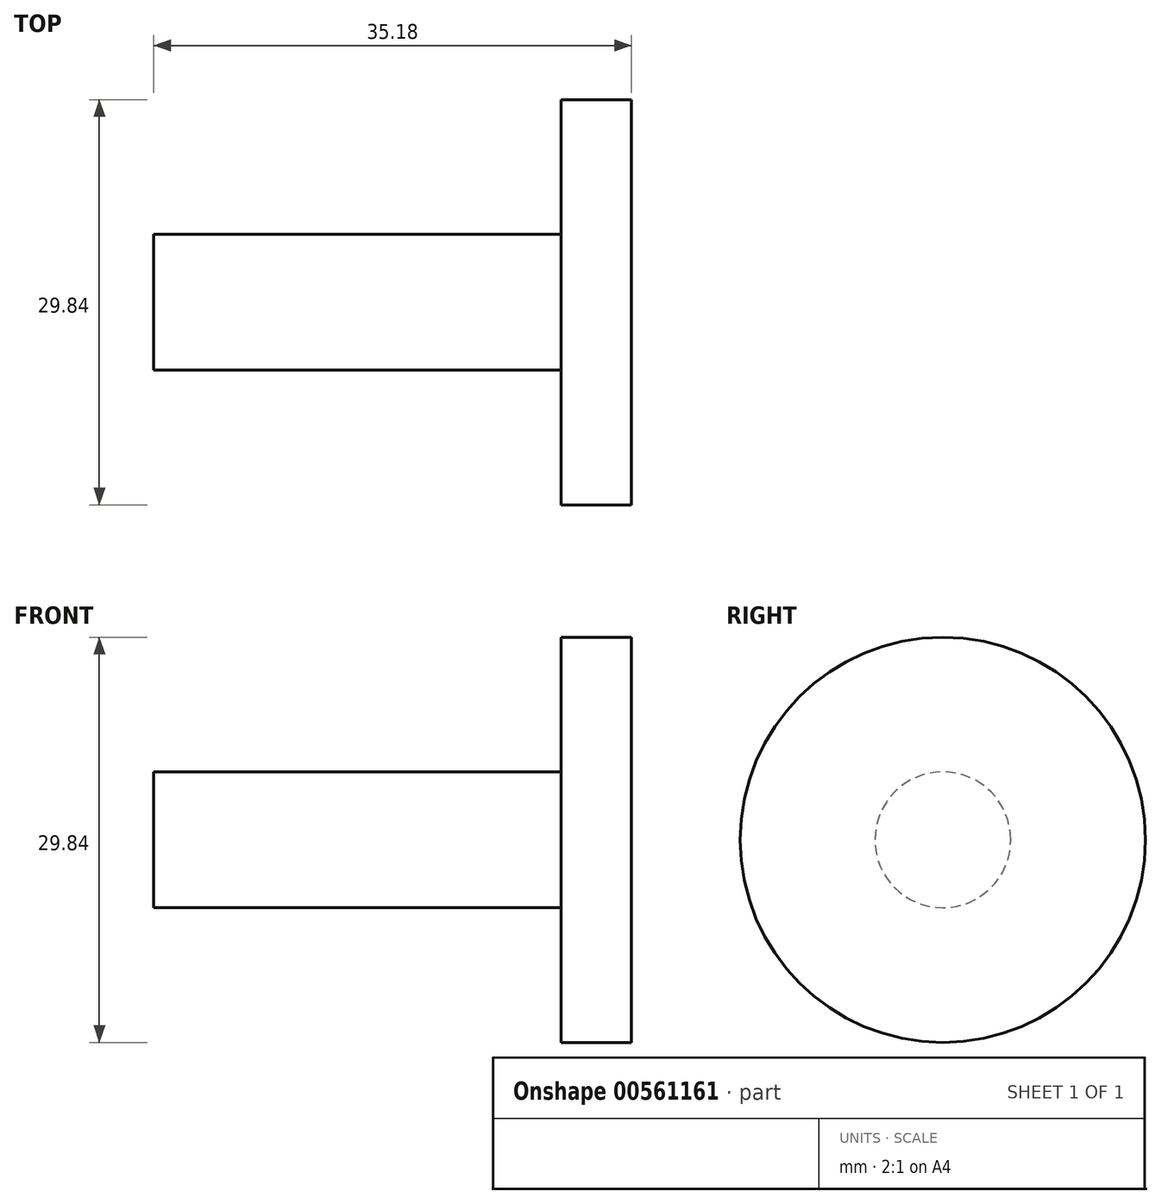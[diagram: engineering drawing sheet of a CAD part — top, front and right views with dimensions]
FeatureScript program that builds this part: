
annotation { "Feature Type Name" : "Feature", "Feature Type Description" : "" }
export const myFeature = defineFeature(function(context is Context, id is Id, definition is map)
    precondition{}
    {
        {
            var Q0;
            Q0=qCreatedBy(makeId("Top.planeOp"),FACE);
            var sketch = newSketch(context, id + "F0", { "sketchPlane" : qUnion([Q0])});
            skLineSegment(sketch, "E0", {"start": v(-30, 0) * mm, "end": v(0, 0) * mm});
            skLineSegment(sketch, "E1.0", {"start": v(-30, -5) * mm, "end": v(0, -5) * mm});
            skLineSegment(sketch, "E2", {"start": v(0, 0) * mm, "end": v(0, 9.92) * mm});
            skLineSegment(sketch, "E3", {"start": v(0, 9.92) * mm, "end": v(5.18, 9.92) * mm});
            skLineSegment(sketch, "E4", {"start": v(5.18, 9.92) * mm, "end": v(5.18, 0) * mm});
            skLineSegment(sketch, "E5", {"start": v(5.18, 0) * mm, "end": v(5.18, -5) * mm});
            skLineSegment(sketch, "E6", {"start": v(5.18, -5) * mm, "end": v(0, -5) * mm});
            skLineSegment(sketch, "E7", {"start": v(-30, -5) * mm, "end": v(-30, 0) * mm});
            skSolve(sketch);
        }
        {
            var Q0;
            Q0 = qSketchRegion(id + "F0", true);
            var Q1;
            Q1=sQuery(id+"F0.wireOp",EDGE,"E6");
            revolve(context, id + "F1", {"entities" : qUnion([Q0]), "axis" : qUnion([Q1]), "revolveType" : RevolveType.FULL});
        }
    });
